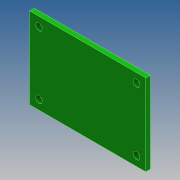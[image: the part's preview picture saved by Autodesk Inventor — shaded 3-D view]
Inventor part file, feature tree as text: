
AUTODESK INVENTOR PART (.ipt)
format: ipt  version: 2017 (Build 210142000, 142)  size: 87,040 bytes
history: native  units: mm
features: other x1, extrude x1, sketch x1
ambient origin geometry x8: Origin, YZ Plane, XZ Plane, XY Plane, X Axis, Y Axis, Z Axis, Center Point
bodies: Body1 (feature_tree)
feature tree (3):
  other  "Sólido1"
  extrude  "Extrusión1"  Depth=2.0mm
  sketch  "Boceto1"  dims[d0=3.0mm d1=4.0mm d2=35.0mm d3=50.0mm d4=2.0mm d5=0.0mm]
